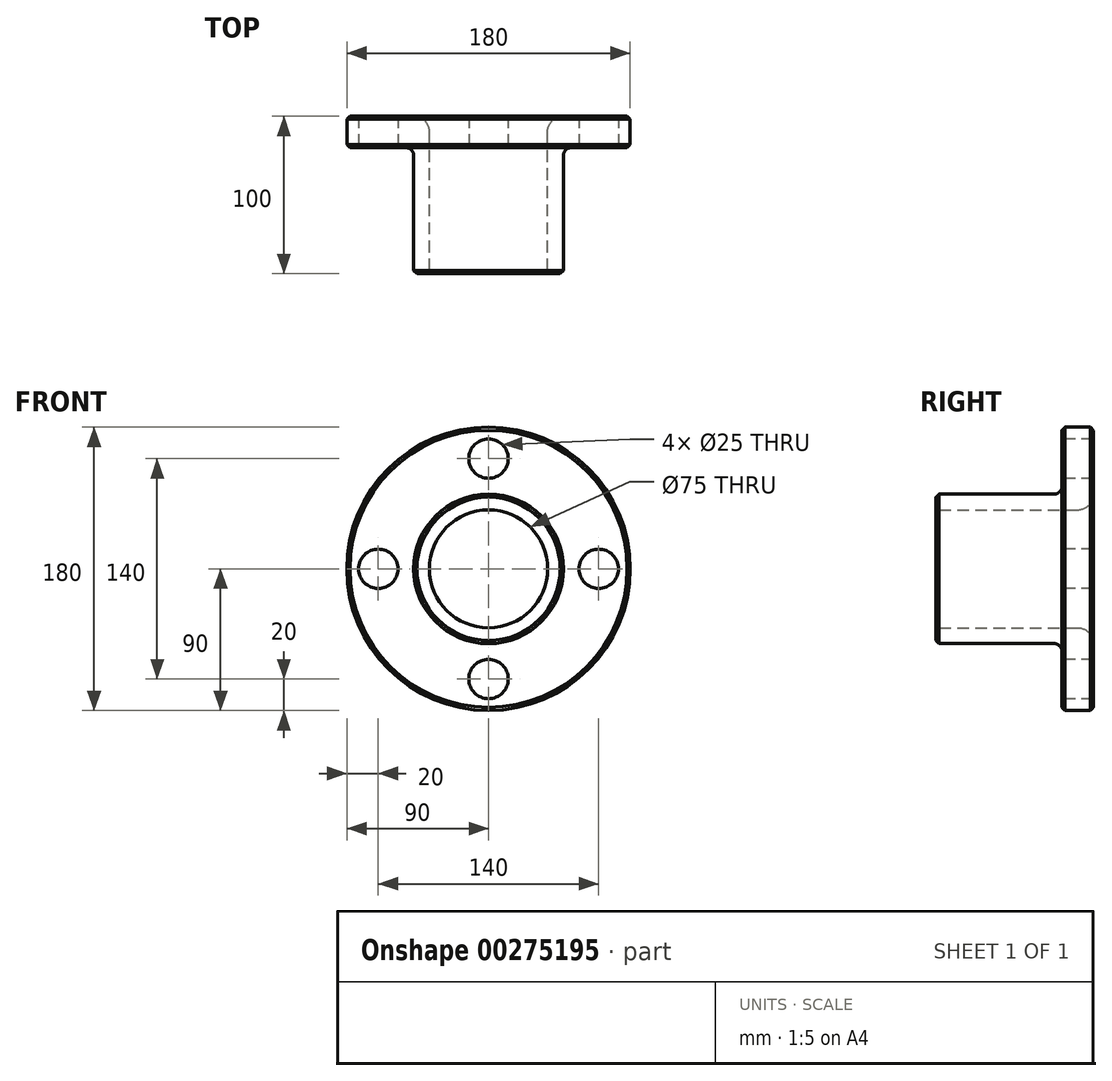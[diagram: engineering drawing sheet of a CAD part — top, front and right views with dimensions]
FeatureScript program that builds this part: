
annotation { "Feature Type Name" : "Feature", "Feature Type Description" : "" }
export const myFeature = defineFeature(function(context is Context, id is Id, definition is map)
    precondition{}
    {
        {
            var Q0;
            Q0=qCreatedBy(makeId("Right.planeOp"),FACE);
            var sketch = newSketch(context, id + "F0", { "sketchPlane" : qUnion([Q0])});
            skLineSegment(sketch, "E0", {"start": v(-100, 47.5) * mm, "end": v(-20, 47.5) * mm});
            skLineSegment(sketch, "E1", {"start": v(-20, 47.5) * mm, "end": v(-20, 90) * mm});
            skLineSegment(sketch, "E2", {"start": v(-20, 90) * mm, "end": v(0, 90) * mm});
            skLineSegment(sketch, "E3", {"start": v(0, 90) * mm, "end": v(0, 37.5) * mm});
            skLineSegment(sketch, "E4", {"start": v(0, 37.5) * mm, "end": v(-100, 37.5) * mm});
            skLineSegment(sketch, "E5", {"start": v(-100, 37.5) * mm, "end": v(-100, 47.5) * mm});
            skLineSegment(sketch, "E6", {"start": v(0, 0) * mm, "end": v(-119.69, 0) * mm, "construction": true});
            skSolve(sketch);
        }
        {
            var Q0;
            Q0 = qSketchRegion(id + "F0", true);
            var Q1;
            Q1=sQuery(id+"F0.wireOp",EDGE,"E6");
            revolve(context, id + "F1", {"entities" : qUnion([Q0]), "axis" : qUnion([Q1]), "revolveType" : RevolveType.FULL});
        }
        {
            var Q0;
            Q0=makeQuery(id+"F1.opRevolve","SWEPT_FACE",FACE,{"disambiguationData":[OSD([sQuery(id+"F0.wireOp",EDGE,"E1")])]});
            var sketch = newSketch(context, id + "F2", { "sketchPlane" : qUnion([Q0])});
            skCircle(sketch, "E7", {"center": v(0, 70) * mm, "radius": 12.5 * mm});
            skCircle(sketch, "E8.1.0", {"center": v(-70, 0) * mm, "radius": 12.5 * mm});
            skCircle(sketch, "E8.2.0", {"center": v(0, -70) * mm, "radius": 12.5 * mm});
            skCircle(sketch, "E8.3.0", {"center": v(70, 0) * mm, "radius": 12.5 * mm});
            skPoint(sketch, "E8.center", {"position": v(0, 0) * mm});
            skSolve(sketch);
        }
        {
            var Q0;
            Q0 = qSketchRegion(id + "F2", true);
            extrude(context, id + "F3", {"entities" : qUnion([Q0]), "operationType" : NewBodyOperationType.REMOVE, "endBound" : BoundingType.UP_TO_NEXT, "oppositeDirection" : true, "depth" : 25 * mm});
        }
        {
            var Q0;
            Q0=makeQuery(id+"F1.opRevolve","SWEPT_EDGE",EDGE,{"disambiguationData":[OSD([sQuery(id+"F0.wireOp",EDGE,"E0"),sQuery(id+"F0.wireOp",EDGE,"E5")])]});
            var Q1;
            Q1=makeQuery(id+"F1.opRevolve","SWEPT_EDGE",EDGE,{"disambiguationData":[OSD([sQuery(id+"F0.wireOp",EDGE,"E1"),sQuery(id+"F0.wireOp",EDGE,"E2")])]});
            var Q2;
            Q2=makeQuery(id+"F1.opRevolve","SWEPT_EDGE",EDGE,{"disambiguationData":[OSD([sQuery(id+"F0.wireOp",EDGE,"E2"),sQuery(id+"F0.wireOp",EDGE,"E3")])]});
            chamfer(context, id + "F4", {"entities" : qUnion([Q0, Q1, Q2]), "width" : 2 * mm, "tangentPropagation" : true});
        }
        {
            var Q0;
            Q0=makeQuery(id+"F1.opRevolve","SWEPT_EDGE",EDGE,{"disambiguationData":[OSD([sQuery(id+"F0.wireOp",EDGE,"E0"),sQuery(id+"F0.wireOp",EDGE,"E1")])]});
            var Q1;
            Q1=makeQuery(id+"F3.boolean.opBoolean","COPY",EDGE,{"derivedFrom":makeQuery(id+"F3.opExtrude","CAP_EDGE",EDGE,{"disambiguationData":[OSD([sQuery(id+"F2.wireOp",EDGE,"E7")])],"isStart":true})});
            var Q2;
            Q2=makeQuery(id+"F3.boolean.opBoolean","COPY",EDGE,{"derivedFrom":makeQuery(id+"F3.opExtrude","CAP_EDGE",EDGE,{"disambiguationData":[OSD([sQuery(id+"F2.wireOp",EDGE,"E8.3.0")])],"isStart":true})});
            var Q3;
            Q3=makeQuery(id+"F3.boolean.opBoolean","COPY",EDGE,{"derivedFrom":makeQuery(id+"F3.opExtrude","CAP_EDGE",EDGE,{"disambiguationData":[OSD([sQuery(id+"F2.wireOp",EDGE,"E8.2.0")])],"isStart":true})});
            var Q4;
            Q4=makeQuery(id+"F3.boolean.opBoolean","COPY",EDGE,{"derivedFrom":makeQuery(id+"F3.opExtrude","CAP_EDGE",EDGE,{"disambiguationData":[OSD([sQuery(id+"F2.wireOp",EDGE,"E8.1.0")])],"isStart":true})});
            var Q5;
            Q5=makeQuery(id+"F3.boolean.opBoolean","COPY",EDGE,{"derivedFrom":makeQuery(id+"F3.opExtrude","CAP_EDGE",EDGE,{"disambiguationData":[OSD([sQuery(id+"F2.wireOp",EDGE,"E8.1.0")])],"isStart":false})});
            var Q6;
            Q6=makeQuery(id+"F3.boolean.opBoolean","COPY",EDGE,{"derivedFrom":makeQuery(id+"F3.opExtrude","CAP_EDGE",EDGE,{"disambiguationData":[OSD([sQuery(id+"F2.wireOp",EDGE,"E7")])],"isStart":false})});
            var Q7;
            Q7=makeQuery(id+"F3.boolean.opBoolean","COPY",EDGE,{"derivedFrom":makeQuery(id+"F3.opExtrude","CAP_EDGE",EDGE,{"disambiguationData":[OSD([sQuery(id+"F2.wireOp",EDGE,"E8.3.0")])],"isStart":false})});
            var Q8;
            Q8=makeQuery(id+"F3.boolean.opBoolean","COPY",EDGE,{"derivedFrom":makeQuery(id+"F3.opExtrude","CAP_EDGE",EDGE,{"disambiguationData":[OSD([sQuery(id+"F2.wireOp",EDGE,"E8.2.0")])],"isStart":false})});
            fillet(context, id + "F5", {"entities" : qUnion([Q0, Q1, Q2, Q3, Q4, Q5, Q6, Q7, Q8]), "radius" : 5 * mm, "tangentPropagation" : true, "allowEdgeOverflow" : false});
        }
        {
            var Q0;
            Q0=makeQuery(id+"F1.opRevolve","SWEPT_EDGE",EDGE,{"disambiguationData":[OSD([sQuery(id+"F0.wireOp",EDGE,"E3"),sQuery(id+"F0.wireOp",EDGE,"E4")])]});
            fillet(context, id + "F6", {"entities" : qUnion([Q0]), "radius" : 10 * mm, "tangentPropagation" : true, "allowEdgeOverflow" : false});
        }
        {
            var Q0;
            Q0=makeQuery(id+"F1.opRevolve","SWEPT_EDGE",EDGE,{"disambiguationData":[OSD([sQuery(id+"F0.wireOp",EDGE,"E4"),sQuery(id+"F0.wireOp",EDGE,"E5")])]});
            fillet(context, id + "F7", {"entities" : qUnion([Q0]), "radius" : 2 * mm, "tangentPropagation" : true, "allowEdgeOverflow" : false});
        }
    });
